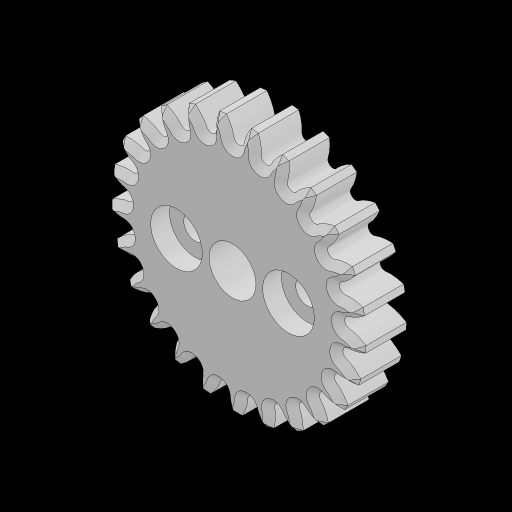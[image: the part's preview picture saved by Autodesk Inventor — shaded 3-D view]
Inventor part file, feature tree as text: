
AUTODESK INVENTOR PART (.ipt)
format: ipt  version: 2023.2 (Build 272271030, 271C)  size: 812,032 bytes
history: native  units: mm
features: sketch x3, extrude x2, chamfer x2, hole x2, pattern_circular x1
ambient origin geometry x8: Origin, YZ Plane, XZ Plane, XY Plane, X Axis, Y Axis, Z Axis, Center Point
bodies: Solid1 (feature_tree)
feature tree (10):
  sketch  "Sketch1"  dims[d0=5.0mm d1=0.0mm]
  extrude  "Extrusion1"  TaperAngle=0.0deg  [1 undecoded]
  extrude  "Extrusion2"  Depth=2.0mm TaperAngle=45.0deg
  chamfer  "Chamfer1"  Distance=2.0mm Angle=45.0deg
  chamfer  "Chamfer2"  Distance=250.0mm Angle=360.0deg
  pattern_circular  "Circular Pattern1"  [2 undecoded]
  sketch  "Sketch2"  dims[d2=0.0mm d3=0.0mm d4=0.7mm d5=2.0mm d6=45.0deg d7=0.7mm d8=2.0mm d9=45.0deg d10=250.0mm d11=360.0deg]
  sketch  "Sketch3"  dims[d13=6.0mm d14=11.9mm d15=20.594885mm d16=90.0deg d17=2.0mm d18=5.5mm d19=8.0mm d20=2.5mm d21=6.0mm d22=20.594885mm d23=90.0deg d24=2.0mm d25=6.0mm d26=8.0mm d27=5.0mm]
  hole  "Hole1"  [1 undecoded]
  hole  "Hole2"  [1 undecoded]
note: 5 required parameter values undecoded (feature->parameter linkage not recoverable at this tier; creation-order binding heuristic only, values carry confidence <= 0.55)
